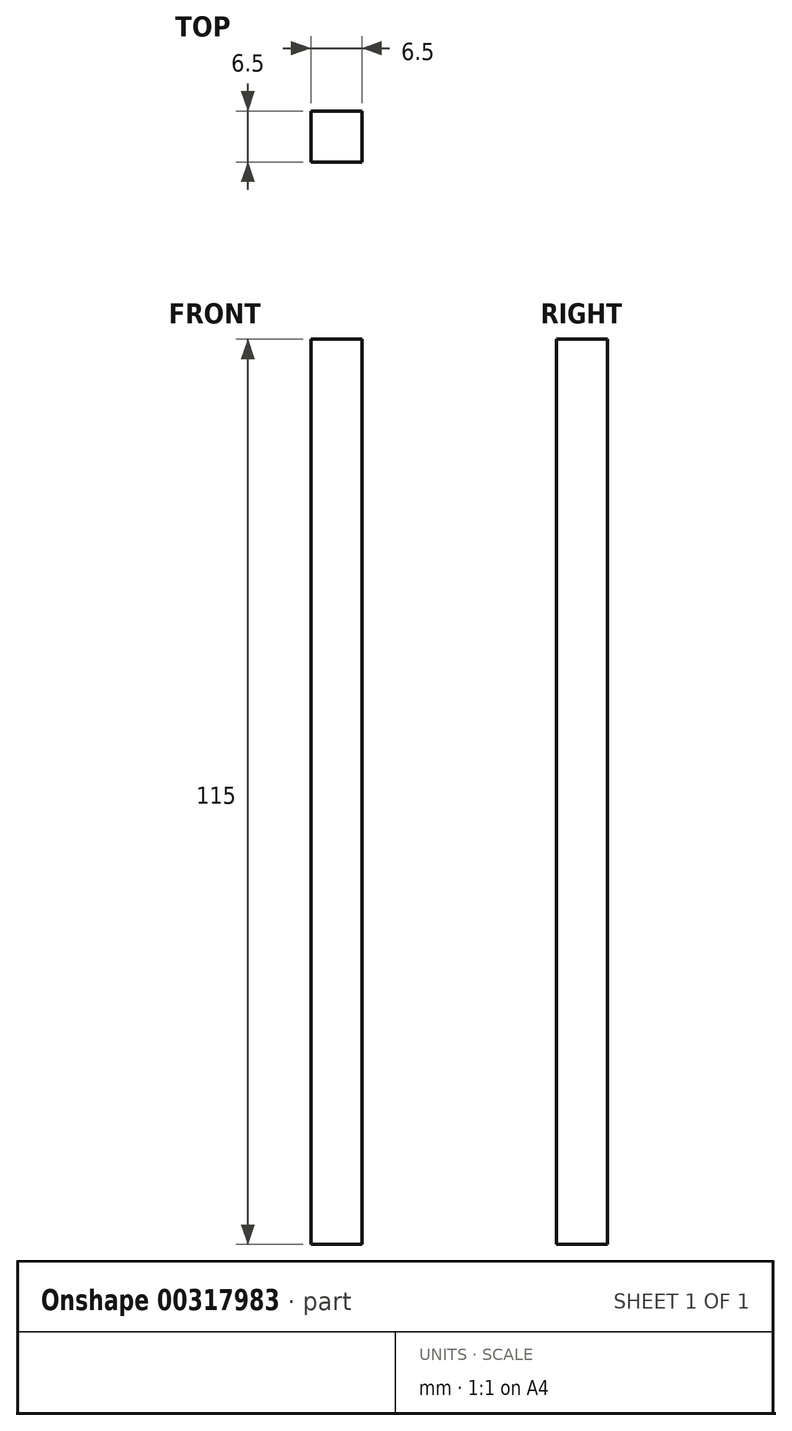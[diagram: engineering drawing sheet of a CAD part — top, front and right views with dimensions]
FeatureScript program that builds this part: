
annotation { "Feature Type Name" : "Feature", "Feature Type Description" : "" }
export const myFeature = defineFeature(function(context is Context, id is Id, definition is map)
    precondition{}
    {
        {
            var Q0;
            Q0=qCreatedBy(makeId("Front.planeOp"),FACE);
            var sketch = newSketch(context, id + "F0", { "sketchPlane" : qUnion([Q0])});
            skLineSegment(sketch, "E0.bottom", {"start": v(-3.25, 57.5) * mm, "end": v(3.25, 57.5) * mm});
            skLineSegment(sketch, "E0.top", {"start": v(-3.25, -57.5) * mm, "end": v(3.25, -57.5) * mm});
            skLineSegment(sketch, "E0.left", {"start": v(-3.25, 57.5) * mm, "end": v(-3.25, -57.5) * mm});
            skLineSegment(sketch, "E0.right", {"start": v(3.25, 57.5) * mm, "end": v(3.25, -57.5) * mm});
            skPoint(sketch, "E0.middle", {"position": v(0, 0) * mm});
            skSolve(sketch);
        }
        {
            var Q0;
            Q0=makeQuery(id+"F0.imprint","IMPRINT",FACE,{"disambiguationData":[TD([[makeQuery(id+"F0.imprint","IMPRINT",EDGE,{"derivedFrom":sQuery(id+"F0.wireOp",EDGE,"E0.bottom")}),-1.0]])]});
            extrude(context, id + "F1", {"entities" : qUnion([Q0]), "depth" : 6.5 * mm});
        }
    });
